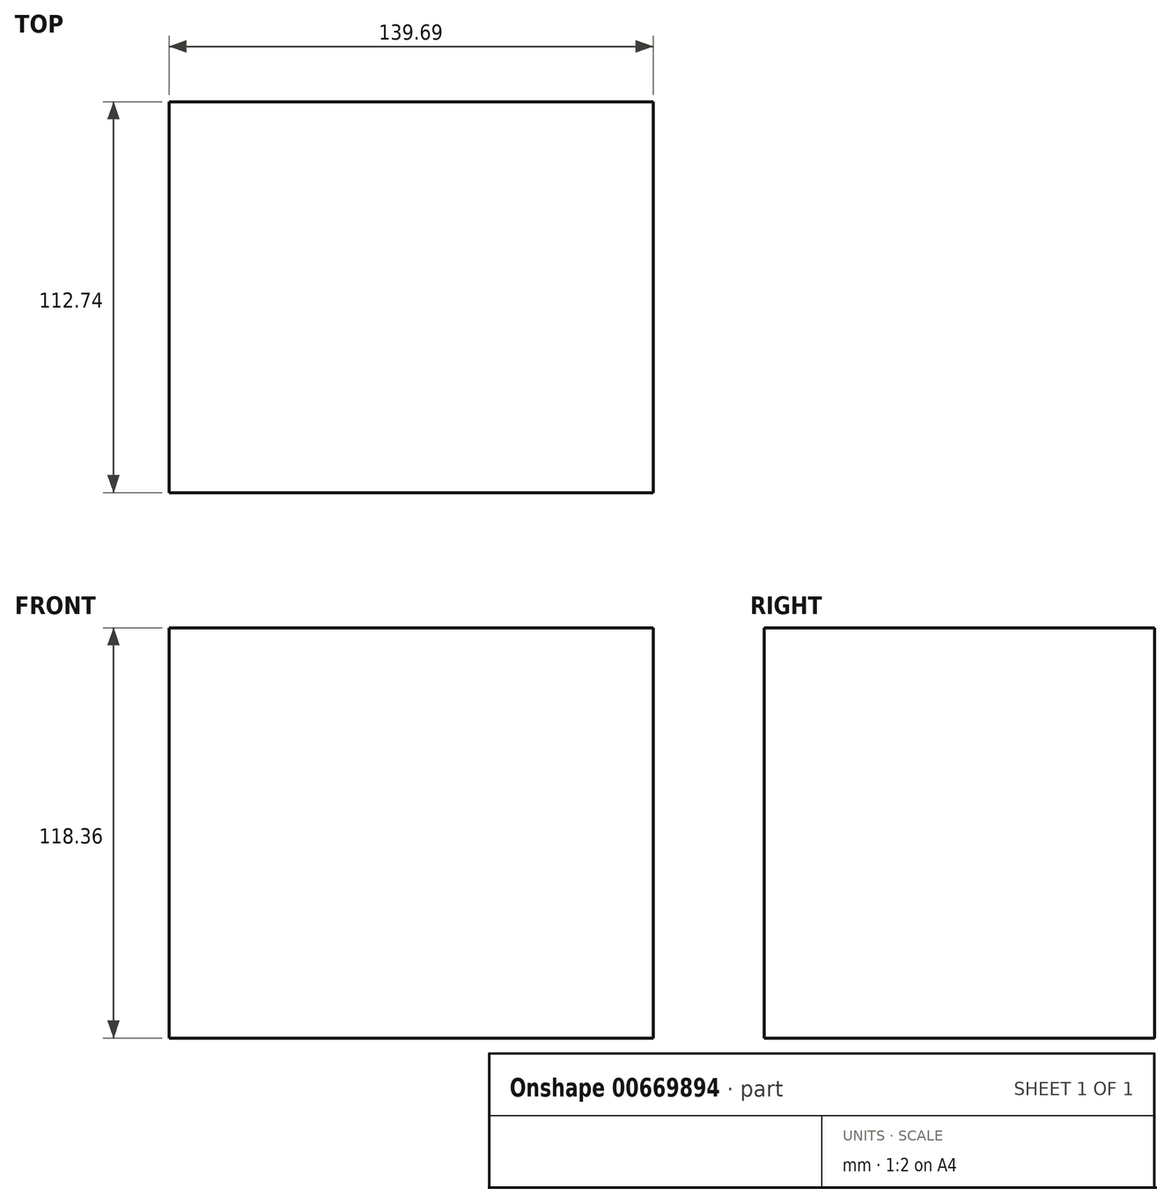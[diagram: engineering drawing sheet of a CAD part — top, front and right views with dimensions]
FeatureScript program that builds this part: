
annotation { "Feature Type Name" : "Feature", "Feature Type Description" : "" }
export const myFeature = defineFeature(function(context is Context, id is Id, definition is map)
    precondition{}
    {
        {
            var Q0;
            Q0=qCreatedBy(makeId("Top.planeOp"),FACE);
            var sketch = newSketch(context, id + "F0", { "sketchPlane" : qUnion([Q0])});
            skLineSegment(sketch, "E0.bottom", {"start": v(-65.86, 58.84) * mm, "end": v(73.83, 58.84) * mm});
            skLineSegment(sketch, "E0.top", {"start": v(-65.86, -53.9) * mm, "end": v(73.83, -53.9) * mm});
            skLineSegment(sketch, "E0.left", {"start": v(-65.86, 58.84) * mm, "end": v(-65.86, -53.9) * mm});
            skLineSegment(sketch, "E0.right", {"start": v(73.83, 58.84) * mm, "end": v(73.83, -53.9) * mm});
            skSolve(sketch);
        }
        {
            var Q0;
            Q0 = qSketchRegion(id + "F0", true);
            extrude(context, id + "F1", {"entities" : qUnion([Q0]), "endBound" : BoundingType.SYMMETRIC, "depth" : 118.36 * mm, "offsetDistance" : 25.4 * mm});
        }
    });
